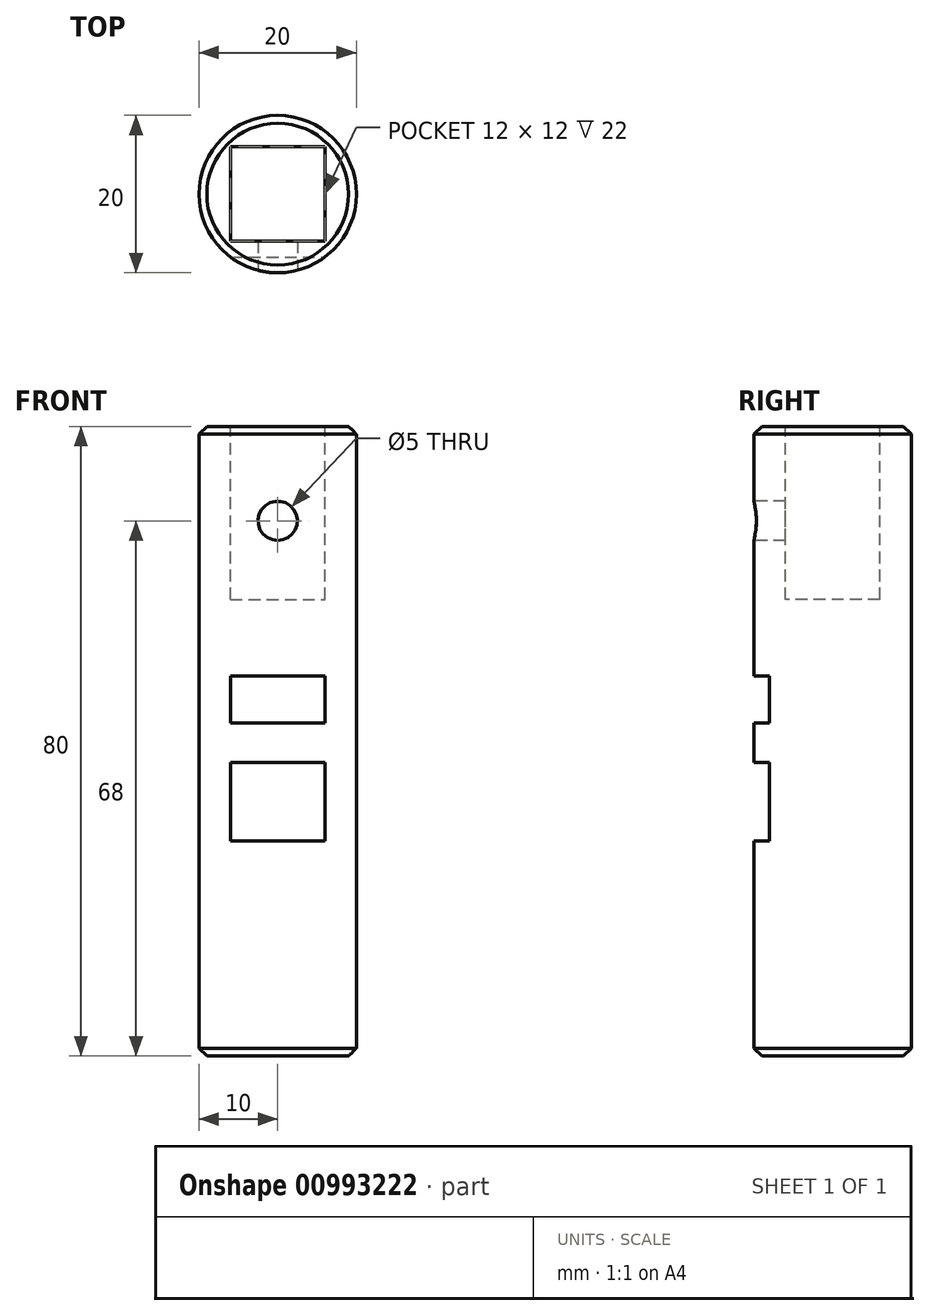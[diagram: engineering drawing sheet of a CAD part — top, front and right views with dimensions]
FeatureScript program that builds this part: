
annotation { "Feature Type Name" : "Feature", "Feature Type Description" : "" }
export const myFeature = defineFeature(function(context is Context, id is Id, definition is map)
    precondition{}
    {
        {
            var Q0;
            Q0=qCreatedBy(makeId("Top.planeOp"),FACE);
            var sketch = newSketch(context, id + "F0", { "sketchPlane" : qUnion([Q0])});
            skCircle(sketch, "E0", {"center": v(0, 0) * mm, "radius": 10 * mm});
            skSolve(sketch);
        }
        {
            var Q0;
            Q0=makeQuery(id+"F0.imprint","IMPRINT",FACE,{"disambiguationData":[TD([[makeQuery(id+"F0.imprint","IMPRINT",EDGE,{"derivedFrom":sQuery(id+"F0.wireOp",EDGE,"E0")}),1.0]])]});
            extrude(context, id + "F1", {"entities" : qUnion([Q0]), "depth" : 80 * mm, "offsetDistance" : 25 * mm});
        }
        {
            var Q0;
            Q0=makeQuery(id+"F1.opExtrude","CAP_FACE",FACE,{"disambiguationData":[OSD([sQuery(id+"F0.wireOp",EDGE,"E0")])],"isStart":false});
            var sketch = newSketch(context, id + "F2", { "sketchPlane" : qUnion([Q0])});
            skLineSegment(sketch, "E1.bottom", {"start": v(-6, 6) * mm, "end": v(6, 6) * mm});
            skLineSegment(sketch, "E1.top", {"start": v(-6, -6) * mm, "end": v(6, -6) * mm});
            skLineSegment(sketch, "E1.left", {"start": v(-6, 6) * mm, "end": v(-6, -6) * mm});
            skLineSegment(sketch, "E1.right", {"start": v(6, 6) * mm, "end": v(6, -6) * mm});
            skSolve(sketch);
        }
        {
            var Q0;
            Q0=makeQuery(id+"F2.imprint","IMPRINT",FACE,{"disambiguationData":[TD([[makeQuery(id+"F2.imprint","IMPRINT",EDGE,{"derivedFrom":sQuery(id+"F2.wireOp",EDGE,"E1.bottom")}),-1.0]])]});
            extrude(context, id + "F3", {"entities" : qUnion([Q0]), "operationType" : NewBodyOperationType.REMOVE, "oppositeDirection" : true, "depth" : 22 * mm, "offsetDistance" : 25 * mm});
        }
        {
            var Q0;
            Q0=qCreatedBy(makeId("Front.planeOp"),FACE);
            cPlane(context, id + "F4", {"entities" : qUnion([Q0]), "cplaneType" : CPlaneType.OFFSET, "offset" : 10 * mm, "width" : 150 * mm, "height" : 150 * mm});
        }
        {
            var Q0;
            Q0=qCreatedBy(id+"F4.planeOp",FACE);
            var sketch = newSketch(context, id + "F5", { "sketchPlane" : qUnion([Q0])});
            skPoint(sketch, "E2", {"position": v(0, 68) * mm});
            skSolve(sketch);
        }
        {
            var Q0;
            Q0=sQuery(id+"F5.wireOp",VERTEX,"E2");
            var Q1;
            Q1=makeQuery(id+"F1.opExtrude","SWEPT_BODY",BODY,{"disambiguationData":[OSD([sQuery(id+"F0.wireOp",EDGE,"E0")])]});
            hole(context, id + "F6", {"style" : HoleStyle.SIMPLE, "endStyle" : HoleEndStyle.BLIND, "holeDiameter" : 5 * mm, "majorDiameter" : 5 * mm, "holeDepth" : 12 * mm, "isTappedThrough" : true, "tappedDepth" : 12 * mm, "tapClearance" : 3, "locations" : qUnion([Q0]), "scope" : qUnion([Q1])});
        }
        {
            var Q0;
            Q0=qCreatedBy(makeId("Right.planeOp"),FACE);
            var sketch = newSketch(context, id + "F7", { "sketchPlane" : qUnion([Q0])});
            skLineSegment(sketch, "E3.bottom", {"start": v(-12, 48.3) * mm, "end": v(-8, 48.3) * mm});
            skLineSegment(sketch, "E3.top", {"start": v(-12, 42.3) * mm, "end": v(-8, 42.3) * mm});
            skLineSegment(sketch, "E3.left", {"start": v(-12, 48.3) * mm, "end": v(-12, 42.3) * mm});
            skLineSegment(sketch, "E3.right", {"start": v(-8, 48.3) * mm, "end": v(-8, 42.3) * mm});
            skLineSegment(sketch, "E4.bottom", {"start": v(-12, 37.3) * mm, "end": v(-8, 37.3) * mm});
            skLineSegment(sketch, "E4.top", {"start": v(-12, 27.3) * mm, "end": v(-8, 27.3) * mm});
            skLineSegment(sketch, "E4.left", {"start": v(-12, 37.3) * mm, "end": v(-12, 27.3) * mm});
            skLineSegment(sketch, "E4.right", {"start": v(-8, 37.3) * mm, "end": v(-8, 27.3) * mm});
            skSolve(sketch);
        }
        {
            var Q0;
            Q0=makeQuery(id+"F7.imprint","IMPRINT",FACE,{"disambiguationData":[TD([[makeQuery(id+"F7.imprint","IMPRINT",EDGE,{"derivedFrom":sQuery(id+"F7.wireOp",EDGE,"E3.bottom")}),-1.0]])]});
            var Q1;
            Q1=makeQuery(id+"F7.imprint","IMPRINT",FACE,{"disambiguationData":[TD([[makeQuery(id+"F7.imprint","IMPRINT",EDGE,{"derivedFrom":sQuery(id+"F7.wireOp",EDGE,"E4.bottom")}),-1.0]])]});
            extrude(context, id + "F8", {"entities" : qUnion([Q0, Q1]), "operationType" : NewBodyOperationType.REMOVE, "endBound" : BoundingType.SYMMETRIC, "oppositeDirection" : true, "depth" : 25 * mm, "offsetDistance" : 25 * mm});
        }
        {
            var Q0;
            Q0=makeQuery(id+"F1.opExtrude","CAP_EDGE",EDGE,{"disambiguationData":[OSD([sQuery(id+"F0.wireOp",EDGE,"E0")])],"isStart":false});
            var Q1;
            Q1=makeQuery(id+"F1.opExtrude","CAP_EDGE",EDGE,{"disambiguationData":[OSD([sQuery(id+"F0.wireOp",EDGE,"E0")])],"isStart":true});
            chamfer(context, id + "F9", {"entities" : qUnion([Q0, Q1]), "width" : 1 * mm, "tangentPropagation" : true});
        }
    });
